# Revit family: Gira_543700
name_source: partatom
category: Electrical Fixtures
revit_build: Autodesk Revit 2017 (Build: 20160225_1515(x64)
units: mm (PartAtom-declared; Revit-internal decimal feet)

## family parameters
Cut with Voids When Loaded = No
Host = Face
Maintain Annotation Orientation = No
Part Type = Normal
Room Calculation Point = No
Round Connector Dimension = Use Diameter
Shared = No

## types (1)
- WL blind act. 1-g DRA Gira eNet
    App control via Bluetooth = No
    Applicable with button = No
    Applicable with infrared button = No
    Applicable with movement sensor = No
    Applicable with presence indicator = No
    Applicable with time switch/timer = No
    Applicable with transmission button = No
    BIM = https://media.live.bim.site X1 REG KNX.rfa
    BIMSITE_PRODUCT_ID = 19f2b6595787a346dbc975ec627ee395b6337b03
    Bus connection included = No
    Cost = 0 $
    Default Elevation = 1219 mm
    Description = WL blind act.1g DRA eNet eNet wireless blind actuator, 1-gang,DRA Features: Can be set with eNet server:: - Fully encrypted wireless transmission (AES CCM) from eNet Server software version 2.0. - Operation locks. - Device software update. - The eNet wireless blind actuator receives telegrams for controlling electrically-operated hangings, e.g. blinds, shutters, or awnings, from the eNet wireless reception module or eNet server via a data cable. - Positioning of blind and slat using scene call-up. - Positions for sun protection and twilight can be saved. - Threshold value scenes for sun protection, twilight and wind alarms. - Status feedback to eNet wireless transmitter. - Hanging period can be saved. - Slat adjustment time can be saved. Can be set with eNet server:: - Adjustment time when changing directions. - Motion direction can be inverted (e.g. for roof windows). - Position for sun protection, twilight, lock-out protection, and wind alarms.,Notes : - An eNet wireless reception module or an eNet server is required to operate this DIN-rail mounting device.
    Dimming phase cut-off = No
    Dimming phase cut-on = No
    GTIN = 4010337774297
    HAN = 543700
    Halogen free = No
    HeinzeBIM = https://www.heinze.de
    Light value memory = No
    Local operation/hand operation = No
    Manufacturer = Gira
    Max. number of venetian-blind outputs = 1
    Max. switching power [Voltampere] = 1000
    Modulare Erweiterungsmöglichkeit = No
    Number of binary inputs = 0
    Number of inputs = 1
    Number of outputs = 0
    Parallel-service possible = No
    Power boost suitable = No
    Radio frequent bidirectional = No
    Serial dimmer = No
    Suitable for C-load = No
    Transparent = No
    URL = https://www.gira.de
    Verschiedene Phasen anschließbar = No
    With label area = No
    With switch function = No

## geometry (parser evidence)
native form markers: Blend x2, Sweep x3
no freeform markers — native parametric forms only
